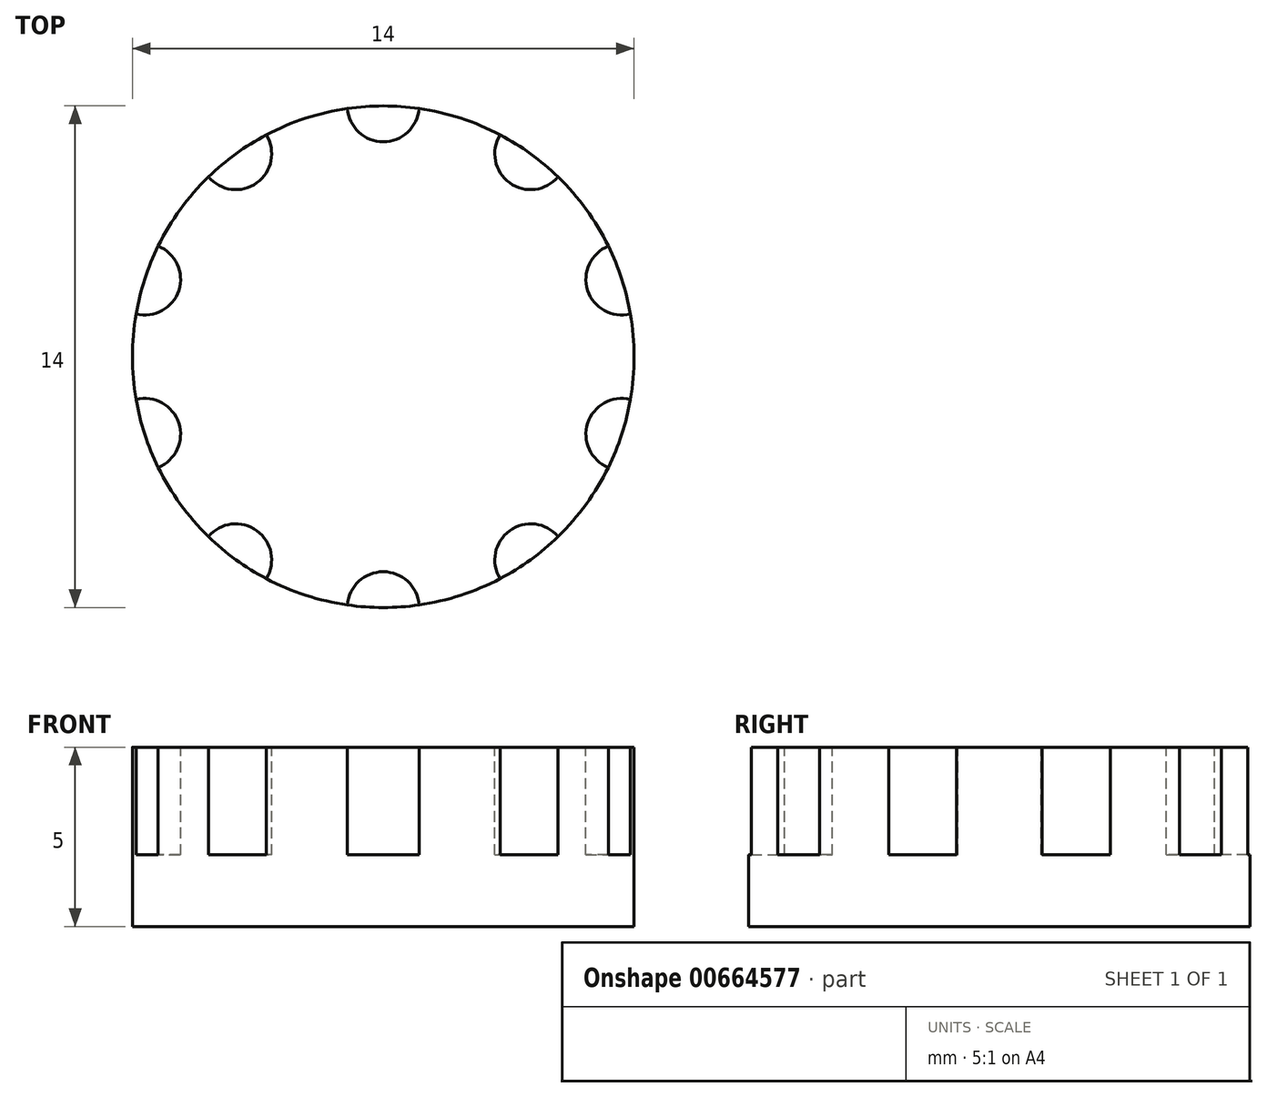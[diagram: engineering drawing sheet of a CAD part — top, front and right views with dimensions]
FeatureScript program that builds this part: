
annotation { "Feature Type Name" : "Feature", "Feature Type Description" : "" }
export const myFeature = defineFeature(function(context is Context, id is Id, definition is map)
    precondition{}
    {
        {
            var Q0;
            Q0=qCreatedBy(makeId("Top.planeOp"),FACE);
            var sketch = newSketch(context, id + "F0", { "sketchPlane" : qUnion([Q0])});
            skCircle(sketch, "E0", {"center": v(0, 0) * mm, "radius": 7 * mm});
            skSolve(sketch);
        }
        {
            var Q0;
            Q0 = qSketchRegion(id + "F0", true);
            extrude(context, id + "F1", {"entities" : qUnion([Q0]), "depth" : 5 * mm, "offsetDistance" : 25 * mm});
        }
        {
            var Q0;
            Q0=makeQuery(id+"F1.opExtrude","CAP_FACE",FACE,{"disambiguationData":[OSD([sQuery(id+"F0.wireOp",EDGE,"E0")])],"isStart":false});
            var sketch = newSketch(context, id + "F2", { "sketchPlane" : qUnion([Q0])});
            skArc(sketch, "E1", {"start": v(-1, 6.93) * mm, "mid": v(0, 6) * mm, "end": v(1, 6.93) * mm});
            skArc(sketch, "E2", {"start": v(1, 6.93) * mm, "mid": v(0, 7) * mm, "end": v(-1, 6.93) * mm});
            skArc(sketch, "E3.1.0", {"start": v(-4.88, 5.02) * mm, "mid": v(-3.53, 4.85) * mm, "end": v(-3.27, 6.2) * mm});
            skArc(sketch, "E3.1.1", {"start": v(-3.27, 6.2) * mm, "mid": v(-4.11, 5.66) * mm, "end": v(-4.88, 5.02) * mm});
            skArc(sketch, "E3.2.0", {"start": v(-6.9, 1.2) * mm, "mid": v(-5.7, 1.85) * mm, "end": v(-6.28, 3.09) * mm});
            skArc(sketch, "E3.2.1", {"start": v(-6.28, 3.09) * mm, "mid": v(-6.66, 2.16) * mm, "end": v(-6.9, 1.2) * mm});
            skArc(sketch, "E3.3.0", {"start": v(-6.28, -3.09) * mm, "mid": v(-5.7, -1.85) * mm, "end": v(-6.9, -1.2) * mm});
            skArc(sketch, "E3.3.1", {"start": v(-6.9, -1.2) * mm, "mid": v(-6.66, -2.16) * mm, "end": v(-6.28, -3.09) * mm});
            skArc(sketch, "E3.4.0", {"start": v(-3.27, -6.2) * mm, "mid": v(-3.53, -4.85) * mm, "end": v(-4.88, -5.02) * mm});
            skArc(sketch, "E3.4.1", {"start": v(-4.88, -5.02) * mm, "mid": v(-4.11, -5.66) * mm, "end": v(-3.27, -6.2) * mm});
            skArc(sketch, "E3.5.0", {"start": v(1, -6.93) * mm, "mid": v(0, -6) * mm, "end": v(-1, -6.93) * mm});
            skArc(sketch, "E3.5.1", {"start": v(-1, -6.93) * mm, "mid": v(0, -7) * mm, "end": v(1, -6.93) * mm});
            skArc(sketch, "E3.6.0", {"start": v(4.88, -5.02) * mm, "mid": v(3.53, -4.85) * mm, "end": v(3.27, -6.2) * mm});
            skArc(sketch, "E3.6.1", {"start": v(3.27, -6.2) * mm, "mid": v(4.11, -5.66) * mm, "end": v(4.88, -5.02) * mm});
            skArc(sketch, "E3.7.0", {"start": v(6.9, -1.2) * mm, "mid": v(5.7, -1.85) * mm, "end": v(6.28, -3.09) * mm});
            skArc(sketch, "E3.7.1", {"start": v(6.28, -3.09) * mm, "mid": v(6.66, -2.16) * mm, "end": v(6.9, -1.2) * mm});
            skArc(sketch, "E3.8.0", {"start": v(6.28, 3.09) * mm, "mid": v(5.7, 1.85) * mm, "end": v(6.9, 1.2) * mm});
            skArc(sketch, "E3.8.1", {"start": v(6.9, 1.2) * mm, "mid": v(6.66, 2.16) * mm, "end": v(6.28, 3.09) * mm});
            skArc(sketch, "E3.9.0", {"start": v(3.27, 6.2) * mm, "mid": v(3.53, 4.85) * mm, "end": v(4.88, 5.02) * mm});
            skArc(sketch, "E3.9.1", {"start": v(4.88, 5.02) * mm, "mid": v(4.11, 5.66) * mm, "end": v(3.27, 6.2) * mm});
            skSolve(sketch);
        }
        {
            var Q0;
            Q0=makeQuery(id+"F2.imprint","IMPRINT",FACE,{"disambiguationData":[TD([[makeQuery(id+"F2.imprint","IMPRINT",EDGE,{"derivedFrom":sQuery(id+"F2.wireOp",EDGE,"E1")}),1.0]])]});
            var Q1;
            Q1=makeQuery(id+"F2.imprint","IMPRINT",FACE,{"disambiguationData":[TD([[makeQuery(id+"F2.imprint","IMPRINT",EDGE,{"derivedFrom":sQuery(id+"F2.wireOp",EDGE,"E3.9.0")}),1.0]])]});
            var Q2;
            Q2=makeQuery(id+"F2.imprint","IMPRINT",FACE,{"disambiguationData":[TD([[makeQuery(id+"F2.imprint","IMPRINT",EDGE,{"derivedFrom":sQuery(id+"F2.wireOp",EDGE,"E3.8.0")}),1.0]])]});
            var Q3;
            Q3=makeQuery(id+"F2.imprint","IMPRINT",FACE,{"disambiguationData":[TD([[makeQuery(id+"F2.imprint","IMPRINT",EDGE,{"derivedFrom":sQuery(id+"F2.wireOp",EDGE,"E3.7.0")}),1.0]])]});
            var Q4;
            Q4=makeQuery(id+"F2.imprint","IMPRINT",FACE,{"disambiguationData":[TD([[makeQuery(id+"F2.imprint","IMPRINT",EDGE,{"derivedFrom":sQuery(id+"F2.wireOp",EDGE,"E3.6.0")}),1.0]])]});
            var Q5;
            Q5=makeQuery(id+"F2.imprint","IMPRINT",FACE,{"disambiguationData":[TD([[makeQuery(id+"F2.imprint","IMPRINT",EDGE,{"derivedFrom":sQuery(id+"F2.wireOp",EDGE,"E3.5.0")}),1.0]])]});
            var Q6;
            Q6=makeQuery(id+"F2.imprint","IMPRINT",FACE,{"disambiguationData":[TD([[makeQuery(id+"F2.imprint","IMPRINT",EDGE,{"derivedFrom":sQuery(id+"F2.wireOp",EDGE,"E3.4.0")}),1.0]])]});
            var Q7;
            Q7=makeQuery(id+"F2.imprint","IMPRINT",FACE,{"disambiguationData":[TD([[makeQuery(id+"F2.imprint","IMPRINT",EDGE,{"derivedFrom":sQuery(id+"F2.wireOp",EDGE,"E3.3.0")}),1.0]])]});
            var Q8;
            Q8=makeQuery(id+"F2.imprint","IMPRINT",FACE,{"disambiguationData":[TD([[makeQuery(id+"F2.imprint","IMPRINT",EDGE,{"derivedFrom":sQuery(id+"F2.wireOp",EDGE,"E3.2.0")}),1.0]])]});
            var Q9;
            Q9=makeQuery(id+"F2.imprint","IMPRINT",FACE,{"disambiguationData":[TD([[makeQuery(id+"F2.imprint","IMPRINT",EDGE,{"derivedFrom":sQuery(id+"F2.wireOp",EDGE,"E3.1.0")}),1.0]])]});
            extrude(context, id + "F3", {"entities" : qUnion([Q0, Q1, Q2, Q3, Q4, Q5, Q6, Q7, Q8, Q9]), "operationType" : NewBodyOperationType.REMOVE, "oppositeDirection" : true, "depth" : 3 * mm, "offsetDistance" : 25 * mm});
        }
    });
